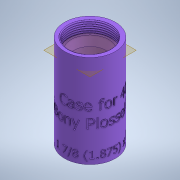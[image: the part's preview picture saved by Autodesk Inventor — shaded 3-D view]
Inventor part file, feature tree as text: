
AUTODESK INVENTOR PART (.ipt)
format: ipt  version: 2021.1 (Build 251245010, 245A)  size: 2,958,336 bytes
history: native  units: in
note: dims shown in document units (in); Inventor stores cm internally (conversion verified against a paired STEP export)
features: sketch x5, emboss x3, plane x2, revolve x1, helix x1, split x1
ambient origin geometry x8: Origin, YZ Plane, XZ Plane, XY Plane, X Axis, Y Axis, Z Axis, Center Point
bodies: Body1 (feature_tree)
feature tree (13):
  revolve  "Revolution2"  [1 undecoded]
  emboss  "Emboss1"
  helix  "Coil6"  [1 undecoded]
  plane  "Work Plane2"
  plane  "Work Plane3"
  emboss  "Emboss2"
  emboss  "Emboss3"
  split  "Split9"
  sketch  "Sketch1"  dims[d0=0.65in d1=1.0in d2=0.685in]
  sketch  "Sketch3"  dims[d3=0.73in]
  sketch  "Sketch11"  dims[d4=0.695in]
  sketch  "Sketch12"  dims[d5=1.21in]
  sketch  "Sketch13"  dims[d6=0.805in d9=0.1875in d14=0.6in d15=0.125in d20=0.35in d23=0.1875in d24=0.9014in d25=0.1875in d26=90.0deg d27=1.6334in d28=0.05in d29=0.0in d82=0.5in d132=60.0deg d133=60.0deg d134=30.0deg d135=0.006in d136=0.0833in d137=30.0deg d138=0.9014in d139=0.0833in d140=0.5833in d141=0.3937in d142=0.0in d143=90.0deg d144=90.0deg d145=0.0in d146=0.0in d147=0.0in d148=3.625in d149=0.05in d150=0.0in d152=0.9494in d153=0.021in d154=0.05in d155=0.0in]
note: 2 required parameter values undecoded (feature->parameter linkage not recoverable at this tier; creation-order binding heuristic only, values carry confidence <= 0.55)